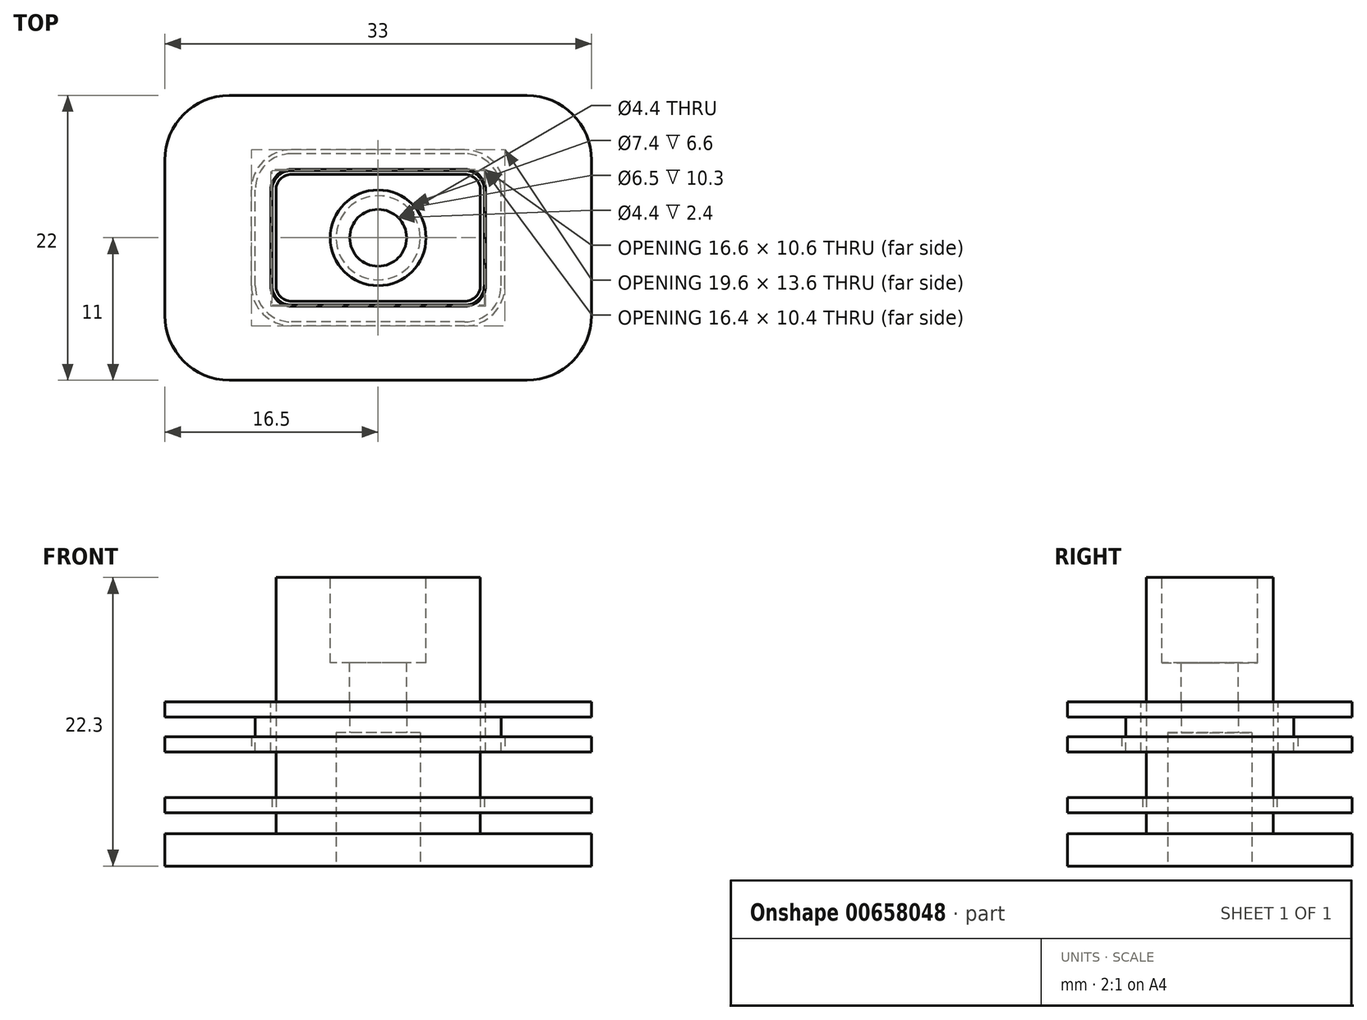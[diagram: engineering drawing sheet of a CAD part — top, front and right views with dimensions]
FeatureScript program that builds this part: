
annotation { "Feature Type Name" : "Feature", "Feature Type Description" : "" }
export const myFeature = defineFeature(function(context is Context, id is Id, definition is map)
    precondition{}
    {
        {
            var Q0;
            Q0=qCreatedBy(makeId("Top.planeOp"),FACE);
            var sketch = newSketch(context, id + "F0", { "sketchPlane" : qUnion([Q0])});
            skLineSegment(sketch, "E0.bottom", {"start": v(16.5, -11) * mm, "end": v(-16.5, -11) * mm});
            skLineSegment(sketch, "E0.top", {"start": v(16.5, 11) * mm, "end": v(-16.5, 11) * mm});
            skLineSegment(sketch, "E0.left", {"start": v(16.5, -11) * mm, "end": v(16.5, 11) * mm});
            skLineSegment(sketch, "E0.right", {"start": v(-16.5, -11) * mm, "end": v(-16.5, 11) * mm});
            skPoint(sketch, "E0.middle", {"position": v(0, 0) * mm});
            skLineSegment(sketch, "E1.bottom", {"start": v(7.9, -4.9) * mm, "end": v(-7.9, -4.9) * mm, "construction": true});
            skLineSegment(sketch, "E1.top", {"start": v(7.9, 4.9) * mm, "end": v(-7.9, 4.9) * mm, "construction": true});
            skLineSegment(sketch, "E1.left", {"start": v(7.9, -4.9) * mm, "end": v(7.9, 4.9) * mm, "construction": true});
            skLineSegment(sketch, "E1.right", {"start": v(-7.9, -4.9) * mm, "end": v(-7.9, 4.9) * mm, "construction": true});
            skCircle(sketch, "E2", {"center": v(0, 0) * mm, "radius": 3.25 * mm});
            skSolve(sketch);
        }
        {
            var Q0;
            Q0 = qSketchRegion(id + "F0", true);
            extrude(context, id + "F1", {"entities" : qUnion([Q0]), "depth" : 2.5 * mm, "offsetDistance" : 25 * mm});
        }
        {
            var Q0;
            Q0=makeQuery(id+"F1.opExtrude","CAP_FACE",FACE,{"disambiguationData":[OSD([sQuery(id+"F0.wireOp",EDGE,"E0.bottom"),sQuery(id+"F0.wireOp",EDGE,"E0.top"),sQuery(id+"F0.wireOp",EDGE,"E0.left"),sQuery(id+"F0.wireOp",EDGE,"E0.right"),sQuery(id+"F0.wireOp",EDGE,"E2")])],"isStart":false});
            var sketch = newSketch(context, id + "F2", { "sketchPlane" : qUnion([Q0])});
            skCircle(sketch, "E3.0", {"center": v(0, 0) * mm, "radius": 3.25 * mm});
            skLineSegment(sketch, "E4.0", {"start": v(7.9, 4.9) * mm, "end": v(-7.9, 4.9) * mm});
            skLineSegment(sketch, "E5.0", {"start": v(7.9, -4.9) * mm, "end": v(7.9, 4.9) * mm});
            skLineSegment(sketch, "E6.0", {"start": v(-7.9, -4.9) * mm, "end": v(-7.9, 4.9) * mm});
            skLineSegment(sketch, "E7.0", {"start": v(7.9, -4.9) * mm, "end": v(-7.9, -4.9) * mm});
            skSolve(sketch);
        }
        {
            var Q0;
            Q0 = qSketchRegion(id + "F2", true);
            extrude(context, id + "F3", {"entities" : qUnion([Q0]), "operationType" : NewBodyOperationType.ADD, "depth" : 7.8 * mm, "offsetDistance" : 25 * mm});
        }
        {
            var Q0;
            Q0=makeQuery(id+"F3.opExtrude","CAP_FACE",FACE,{"disambiguationData":[OSD([sQuery(id+"F2.wireOp",EDGE,"E3.0"),sQuery(id+"F2.wireOp",EDGE,"E4.0"),sQuery(id+"F2.wireOp",EDGE,"E5.0"),sQuery(id+"F2.wireOp",EDGE,"E6.0"),sQuery(id+"F2.wireOp",EDGE,"E7.0")])],"isStart":false});
            var sketch = newSketch(context, id + "F4", { "sketchPlane" : qUnion([Q0])});
            skLineSegment(sketch, "E8.0.0", {"start": v(-7.9, -4.9) * mm, "end": v(7.9, -4.9) * mm});
            skLineSegment(sketch, "E8.0.1", {"start": v(7.9, -4.9) * mm, "end": v(7.9, 4.9) * mm});
            skLineSegment(sketch, "E8.0.2", {"start": v(7.9, 4.9) * mm, "end": v(-7.9, 4.9) * mm});
            skLineSegment(sketch, "E8.0.3", {"start": v(-7.9, 4.9) * mm, "end": v(-7.9, -4.9) * mm});
            skCircle(sketch, "E9", {"center": v(0, 0) * mm, "radius": 2.2 * mm});
            skSolve(sketch);
        }
        {
            var Q0;
            Q0 = qSketchRegion(id + "F4", true);
            extrude(context, id + "F5", {"entities" : qUnion([Q0]), "operationType" : NewBodyOperationType.ADD, "depth" : 2.4 * mm, "offsetDistance" : 25 * mm});
        }
        {
            var Q0;
            Q0=makeQuery(id+"F5.opExtrude","CAP_FACE",FACE,{"disambiguationData":[OSD([sQuery(id+"F4.wireOp",EDGE,"E8.0.0"),sQuery(id+"F4.wireOp",EDGE,"E8.0.1"),sQuery(id+"F4.wireOp",EDGE,"E8.0.2"),sQuery(id+"F4.wireOp",EDGE,"E8.0.3"),sQuery(id+"F4.wireOp",EDGE,"E9")])],"isStart":false});
            var sketch = newSketch(context, id + "F6", { "sketchPlane" : qUnion([Q0])});
            skLineSegment(sketch, "E10.0.0", {"start": v(-7.9, -4.9) * mm, "end": v(7.9, -4.9) * mm});
            skLineSegment(sketch, "E10.0.1", {"start": v(7.9, -4.9) * mm, "end": v(7.9, 4.9) * mm});
            skLineSegment(sketch, "E10.0.2", {"start": v(7.9, 4.9) * mm, "end": v(-7.9, 4.9) * mm});
            skLineSegment(sketch, "E10.0.3", {"start": v(-7.9, 4.9) * mm, "end": v(-7.9, -4.9) * mm});
            skSolve(sketch);
        }
        {
            var Q0;
            Q0 = qSketchRegion(id + "F6", true);
            extrude(context, id + "F7", {"entities" : qUnion([Q0]), "depth" : 9.6 * mm, "offsetDistance" : 25 * mm});
        }
        {
            var Q0;
            Q0=makeQuery(id+"F7.opExtrude","CAP_FACE",FACE,{"disambiguationData":[OSD([sQuery(id+"F6.wireOp",EDGE,"E10.0.0"),sQuery(id+"F6.wireOp",EDGE,"E10.0.1"),sQuery(id+"F6.wireOp",EDGE,"E10.0.2"),sQuery(id+"F6.wireOp",EDGE,"E10.0.3")])],"isStart":false});
            var sketch = newSketch(context, id + "F8", { "sketchPlane" : qUnion([Q0])});
            skPoint(sketch, "E11", {"position": v(0, 0) * mm});
            skSolve(sketch);
        }
        {
            var Q0;
            Q0=sQuery(id+"F8.wireOp",VERTEX,"E11");
            var Q1;
            Q1=makeQuery(id+"F7.opExtrude","SWEPT_BODY",BODY,{"disambiguationData":[OSD([sQuery(id+"F6.wireOp",EDGE,"E10.0.0"),sQuery(id+"F6.wireOp",EDGE,"E10.0.1"),sQuery(id+"F6.wireOp",EDGE,"E10.0.2"),sQuery(id+"F6.wireOp",EDGE,"E10.0.3")])]});
            hole(context, id + "F9", {"style" : HoleStyle.C_BORE, "endStyle" : HoleEndStyle.THROUGH, "holeDiameter" : 4.4 * mm, "cBoreDiameter" : 7.4 * mm, "cBoreDepth" : 6.6 * mm, "majorDiameter" : 5 * mm, "tappedDepth" : 5 * mm, "tapClearance" : 6, "startFromSketch" : true, "locations" : qUnion([Q0]), "scope" : qUnion([Q1])});
        }
        {
            var Q0;
            Q0=makeQuery(id+"F1.opExtrude","SWEPT_EDGE",EDGE,{"disambiguationData":[OSD([sQuery(id+"F0.wireOp",EDGE,"E0.bottom"),sQuery(id+"F0.wireOp",EDGE,"E0.left")])]});
            var Q1;
            Q1=makeQuery(id+"F1.opExtrude","SWEPT_EDGE",EDGE,{"disambiguationData":[OSD([sQuery(id+"F0.wireOp",EDGE,"E0.top"),sQuery(id+"F0.wireOp",EDGE,"E0.left")])]});
            var Q2;
            Q2=makeQuery(id+"F1.opExtrude","SWEPT_EDGE",EDGE,{"disambiguationData":[OSD([sQuery(id+"F0.wireOp",EDGE,"E0.bottom"),sQuery(id+"F0.wireOp",EDGE,"E0.right")])]});
            var Q3;
            Q3=makeQuery(id+"F1.opExtrude","SWEPT_EDGE",EDGE,{"disambiguationData":[OSD([sQuery(id+"F0.wireOp",EDGE,"E0.top"),sQuery(id+"F0.wireOp",EDGE,"E0.right")])]});
            fillet(context, id + "F10", {"entities" : qUnion([Q0, Q1, Q2, Q3]), "radius" : 5 * mm, "tangentPropagation" : true, "allowEdgeOverflow" : false});
        }
        {
            var Q0;
            Q0=makeQuery(id+"F5.boolean.opBoolean","MERGE",EDGE,{"derivedFrom":[makeQuery(id+"F3.opExtrude","SWEPT_EDGE",EDGE,{"disambiguationData":[OSD([sQuery(id+"F2.wireOp",EDGE,"E4.0"),sQuery(id+"F2.wireOp",EDGE,"E6.0")])]}),makeQuery(id+"F5.opExtrude","SWEPT_EDGE",EDGE,{"disambiguationData":[OSD([sQuery(id+"F4.wireOp",EDGE,"E8.0.2"),sQuery(id+"F4.wireOp",EDGE,"E8.0.3")])]})]});
            var Q1;
            Q1=makeQuery(id+"F5.boolean.opBoolean","MERGE",EDGE,{"derivedFrom":[makeQuery(id+"F3.opExtrude","SWEPT_EDGE",EDGE,{"disambiguationData":[OSD([sQuery(id+"F2.wireOp",EDGE,"E6.0"),sQuery(id+"F2.wireOp",EDGE,"E7.0")])]}),makeQuery(id+"F5.opExtrude","SWEPT_EDGE",EDGE,{"disambiguationData":[OSD([sQuery(id+"F4.wireOp",EDGE,"E8.0.0"),sQuery(id+"F4.wireOp",EDGE,"E8.0.3")])]})]});
            var Q2;
            Q2=makeQuery(id+"F5.boolean.opBoolean","MERGE",EDGE,{"derivedFrom":[makeQuery(id+"F3.opExtrude","SWEPT_EDGE",EDGE,{"disambiguationData":[OSD([sQuery(id+"F2.wireOp",EDGE,"E4.0"),sQuery(id+"F2.wireOp",EDGE,"E5.0")])]}),makeQuery(id+"F5.opExtrude","SWEPT_EDGE",EDGE,{"disambiguationData":[OSD([sQuery(id+"F4.wireOp",EDGE,"E8.0.1"),sQuery(id+"F4.wireOp",EDGE,"E8.0.2")])]})]});
            var Q3;
            Q3=makeQuery(id+"F5.boolean.opBoolean","MERGE",EDGE,{"derivedFrom":[makeQuery(id+"F3.opExtrude","SWEPT_EDGE",EDGE,{"disambiguationData":[OSD([sQuery(id+"F2.wireOp",EDGE,"E5.0"),sQuery(id+"F2.wireOp",EDGE,"E7.0")])]}),makeQuery(id+"F5.opExtrude","SWEPT_EDGE",EDGE,{"disambiguationData":[OSD([sQuery(id+"F4.wireOp",EDGE,"E8.0.0"),sQuery(id+"F4.wireOp",EDGE,"E8.0.1")])]})]});
            var Q4;
            Q4=makeQuery(id+"F7.opExtrude","SWEPT_EDGE",EDGE,{"disambiguationData":[OSD([sQuery(id+"F6.wireOp",EDGE,"E10.0.1"),sQuery(id+"F6.wireOp",EDGE,"E10.0.2")])]});
            var Q5;
            Q5=makeQuery(id+"F7.opExtrude","SWEPT_EDGE",EDGE,{"disambiguationData":[OSD([sQuery(id+"F6.wireOp",EDGE,"E10.0.0"),sQuery(id+"F6.wireOp",EDGE,"E10.0.1")])]});
            var Q6;
            Q6=makeQuery(id+"F7.opExtrude","SWEPT_EDGE",EDGE,{"disambiguationData":[OSD([sQuery(id+"F6.wireOp",EDGE,"E10.0.2"),sQuery(id+"F6.wireOp",EDGE,"E10.0.3")])]});
            var Q7;
            Q7=makeQuery(id+"F7.opExtrude","SWEPT_EDGE",EDGE,{"disambiguationData":[OSD([sQuery(id+"F6.wireOp",EDGE,"E10.0.0"),sQuery(id+"F6.wireOp",EDGE,"E10.0.3")])]});
            fillet(context, id + "F11", {"entities" : qUnion([Q0, Q1, Q2, Q3, Q4, Q5, Q6, Q7]), "radius" : 1.2 * mm, "tangentPropagation" : true, "allowEdgeOverflow" : false});
        }
        {
            var Q0;
            Q0=makeQuery(id+"F5.opExtrude","CAP_FACE",FACE,{"disambiguationData":[OSD([sQuery(id+"F4.wireOp",EDGE,"E8.0.0"),sQuery(id+"F4.wireOp",EDGE,"E8.0.1"),sQuery(id+"F4.wireOp",EDGE,"E8.0.2"),sQuery(id+"F4.wireOp",EDGE,"E8.0.3"),sQuery(id+"F4.wireOp",EDGE,"E9")])],"isStart":false});
            var sketch = newSketch(context, id + "F12", { "sketchPlane" : qUnion([Q0])});
            skLineSegment(sketch, "E12.0", {"start": v(6.7, 5.3) * mm, "end": v(-6.7, 5.3) * mm});
            skArc(sketch, "E12.1", {"start": v(8.3, 3.7) * mm, "mid": v(7.83, 4.83) * mm, "end": v(6.7, 5.3) * mm});
            skArc(sketch, "E12.2", {"start": v(-6.7, 5.3) * mm, "mid": v(-7.83, 4.83) * mm, "end": v(-8.3, 3.7) * mm});
            skLineSegment(sketch, "E12.3", {"start": v(8.3, -3.7) * mm, "end": v(8.3, 3.7) * mm});
            skLineSegment(sketch, "E12.4", {"start": v(-8.3, -3.7) * mm, "end": v(-8.3, 3.7) * mm});
            skArc(sketch, "E12.5", {"start": v(-8.3, -3.7) * mm, "mid": v(-7.83, -4.83) * mm, "end": v(-6.7, -5.3) * mm});
            skLineSegment(sketch, "E12.6", {"start": v(6.7, -5.3) * mm, "end": v(-6.7, -5.3) * mm});
            skArc(sketch, "E12.7", {"start": v(6.7, -5.3) * mm, "mid": v(7.83, -4.83) * mm, "end": v(8.3, -3.7) * mm});
            skArc(sketch, "E13.0", {"start": v(-11.5, 11) * mm, "mid": v(-15.04, 9.54) * mm, "end": v(-16.5, 6) * mm});
            skLineSegment(sketch, "E14.0", {"start": v(11.5, 11) * mm, "end": v(-11.5, 11) * mm});
            skLineSegment(sketch, "E15.0", {"start": v(-16.5, -6) * mm, "end": v(-16.5, 6) * mm});
            skArc(sketch, "E16.0", {"start": v(16.5, 6) * mm, "mid": v(15.04, 9.54) * mm, "end": v(11.5, 11) * mm});
            skLineSegment(sketch, "E17.0", {"start": v(16.5, -6) * mm, "end": v(16.5, 6) * mm});
            skArc(sketch, "E18.0", {"start": v(11.5, -11) * mm, "mid": v(15.04, -9.54) * mm, "end": v(16.5, -6) * mm});
            skLineSegment(sketch, "E19.0", {"start": v(11.5, -11) * mm, "end": v(-11.5, -11) * mm});
            skArc(sketch, "E20.0", {"start": v(-16.5, -6) * mm, "mid": v(-15.04, -9.54) * mm, "end": v(-11.5, -11) * mm});
            skSolve(sketch);
        }
        {
            var Q0;
            Q0 = qSketchRegion(id + "F12", true);
            extrude(context, id + "F13", {"entities" : qUnion([Q0]), "oppositeDirection" : true, "depth" : 1.2 * mm, "offsetDistance" : 25 * mm});
        }
        {
            var Q0;
            Q0=makeQuery(id+"F13.opExtrude","CAP_FACE",FACE,{"disambiguationData":[OSD([sQuery(id+"F12.wireOp",EDGE,"E12.0"),sQuery(id+"F12.wireOp",EDGE,"E12.1"),sQuery(id+"F12.wireOp",EDGE,"E12.2"),sQuery(id+"F12.wireOp",EDGE,"E12.3"),sQuery(id+"F12.wireOp",EDGE,"E12.4"),sQuery(id+"F12.wireOp",EDGE,"E12.5"),sQuery(id+"F12.wireOp",EDGE,"E12.6"),sQuery(id+"F12.wireOp",EDGE,"E12.7"),sQuery(id+"F12.wireOp",EDGE,"E13.0"),sQuery(id+"F12.wireOp",EDGE,"E14.0"),sQuery(id+"F12.wireOp",EDGE,"E15.0"),sQuery(id+"F12.wireOp",EDGE,"E16.0"),sQuery(id+"F12.wireOp",EDGE,"E17.0"),sQuery(id+"F12.wireOp",EDGE,"E18.0"),sQuery(id+"F12.wireOp",EDGE,"E19.0"),sQuery(id+"F12.wireOp",EDGE,"E20.0")])],"isStart":false});
            var sketch = newSketch(context, id + "F14", { "sketchPlane" : qUnion([Q0])});
            skLineSegment(sketch, "E21.0", {"start": v(-9.5, 3.7) * mm, "end": v(-9.5, -3.7) * mm});
            skArc(sketch, "E21.1", {"start": v(-6.7, -6.5) * mm, "mid": v(-8.68, -5.68) * mm, "end": v(-9.5, -3.7) * mm});
            skArc(sketch, "E21.2", {"start": v(-9.5, 3.7) * mm, "mid": v(-8.68, 5.68) * mm, "end": v(-6.7, 6.5) * mm});
            skLineSegment(sketch, "E21.3", {"start": v(6.7, -6.5) * mm, "end": v(-6.7, -6.5) * mm});
            skLineSegment(sketch, "E21.4", {"start": v(6.7, 6.5) * mm, "end": v(-6.7, 6.5) * mm});
            skArc(sketch, "E21.5", {"start": v(6.7, 6.5) * mm, "mid": v(8.68, 5.68) * mm, "end": v(9.5, 3.7) * mm});
            skLineSegment(sketch, "E21.6", {"start": v(9.5, 3.7) * mm, "end": v(9.5, -3.7) * mm});
            skArc(sketch, "E21.7", {"start": v(9.5, -3.7) * mm, "mid": v(8.68, -5.68) * mm, "end": v(6.7, -6.5) * mm});
            skLineSegment(sketch, "E22.0", {"start": v(6.7, 5.3) * mm, "end": v(-6.7, 5.3) * mm});
            skArc(sketch, "E23.0", {"start": v(-8.3, 3.7) * mm, "mid": v(-7.83, 4.83) * mm, "end": v(-6.7, 5.3) * mm});
            skLineSegment(sketch, "E24.0", {"start": v(-8.3, 3.7) * mm, "end": v(-8.3, -3.7) * mm});
            skArc(sketch, "E25.0", {"start": v(-6.7, -5.3) * mm, "mid": v(-7.83, -4.83) * mm, "end": v(-8.3, -3.7) * mm});
            skLineSegment(sketch, "E26.0", {"start": v(6.7, -5.3) * mm, "end": v(-6.7, -5.3) * mm});
            skArc(sketch, "E27.0", {"start": v(8.3, -3.7) * mm, "mid": v(7.83, -4.83) * mm, "end": v(6.7, -5.3) * mm});
            skLineSegment(sketch, "E28.0", {"start": v(8.3, 3.7) * mm, "end": v(8.3, -3.7) * mm});
            skArc(sketch, "E29.0", {"start": v(6.7, 5.3) * mm, "mid": v(7.83, 4.83) * mm, "end": v(8.3, 3.7) * mm});
            skSolve(sketch);
        }
        {
            var Q0;
            Q0 = qSketchRegion(id + "F14", true);
            extrude(context, id + "F15", {"entities" : qUnion([Q0]), "operationType" : NewBodyOperationType.ADD, "depth" : 2.7 * mm, "offsetDistance" : 25 * mm});
        }
        {
            var Q0;
            Q0=makeQuery(id+"F15.opExtrude","CAP_FACE",FACE,{"disambiguationData":[OSD([sQuery(id+"F14.wireOp",EDGE,"E21.0"),sQuery(id+"F14.wireOp",EDGE,"E21.1"),sQuery(id+"F14.wireOp",EDGE,"E21.2"),sQuery(id+"F14.wireOp",EDGE,"E21.3"),sQuery(id+"F14.wireOp",EDGE,"E21.4"),sQuery(id+"F14.wireOp",EDGE,"E21.5"),sQuery(id+"F14.wireOp",EDGE,"E21.6"),sQuery(id+"F14.wireOp",EDGE,"E21.7"),sQuery(id+"F14.wireOp",EDGE,"E22.0"),sQuery(id+"F14.wireOp",EDGE,"E23.0"),sQuery(id+"F14.wireOp",EDGE,"E24.0"),sQuery(id+"F14.wireOp",EDGE,"E25.0"),sQuery(id+"F14.wireOp",EDGE,"E26.0"),sQuery(id+"F14.wireOp",EDGE,"E27.0"),sQuery(id+"F14.wireOp",EDGE,"E28.0"),sQuery(id+"F14.wireOp",EDGE,"E29.0")])],"isStart":false});
            var sketch = newSketch(context, id + "F16", { "sketchPlane" : qUnion([Q0])});
            skArc(sketch, "E30.0", {"start": v(6.7, 6.8) * mm, "mid": v(8.9, 5.9) * mm, "end": v(9.8, 3.7) * mm});
            skLineSegment(sketch, "E30.1", {"start": v(6.7, 6.8) * mm, "end": v(-6.7, 6.8) * mm});
            skLineSegment(sketch, "E30.2", {"start": v(9.8, 3.7) * mm, "end": v(9.8, -3.7) * mm});
            skArc(sketch, "E30.3", {"start": v(-9.8, 3.7) * mm, "mid": v(-8.9, 5.9) * mm, "end": v(-6.7, 6.8) * mm});
            skArc(sketch, "E30.4", {"start": v(9.8, -3.7) * mm, "mid": v(8.9, -5.9) * mm, "end": v(6.7, -6.8) * mm});
            skLineSegment(sketch, "E30.5", {"start": v(6.7, -6.8) * mm, "end": v(-6.7, -6.8) * mm});
            skArc(sketch, "E30.6", {"start": v(-6.7, -6.8) * mm, "mid": v(-8.9, -5.9) * mm, "end": v(-9.8, -3.7) * mm});
            skLineSegment(sketch, "E30.7", {"start": v(-9.8, 3.7) * mm, "end": v(-9.8, -3.7) * mm});
            skArc(sketch, "E31.0", {"start": v(-16.5, 6) * mm, "mid": v(-15.04, 9.54) * mm, "end": v(-11.5, 11) * mm});
            skLineSegment(sketch, "E32.0", {"start": v(-16.5, 6) * mm, "end": v(-16.5, -6) * mm});
            skLineSegment(sketch, "E33.0", {"start": v(11.5, 11) * mm, "end": v(-11.5, 11) * mm});
            skArc(sketch, "E34.0", {"start": v(11.5, 11) * mm, "mid": v(15.04, 9.54) * mm, "end": v(16.5, 6) * mm});
            skLineSegment(sketch, "E35.0", {"start": v(16.5, 6) * mm, "end": v(16.5, -6) * mm});
            skArc(sketch, "E36.0", {"start": v(16.5, -6) * mm, "mid": v(15.04, -9.54) * mm, "end": v(11.5, -11) * mm});
            skLineSegment(sketch, "E37.0", {"start": v(11.5, -11) * mm, "end": v(-11.5, -11) * mm});
            skArc(sketch, "E38.0", {"start": v(-11.5, -11) * mm, "mid": v(-15.04, -9.54) * mm, "end": v(-16.5, -6) * mm});
            skSolve(sketch);
        }
        {
            var Q0;
            Q0 = qSketchRegion(id + "F16", true);
            extrude(context, id + "F17", {"entities" : qUnion([Q0]), "oppositeDirection" : true, "depth" : 1.2 * mm, "offsetDistance" : 25 * mm});
        }
        {
            var Q0;
            Q0=makeQuery(id+"F1.opExtrude","CAP_FACE",FACE,{"disambiguationData":[OSD([sQuery(id+"F0.wireOp",EDGE,"E0.bottom"),sQuery(id+"F0.wireOp",EDGE,"E0.top"),sQuery(id+"F0.wireOp",EDGE,"E0.left"),sQuery(id+"F0.wireOp",EDGE,"E0.right"),sQuery(id+"F0.wireOp",EDGE,"E2")])],"isStart":false});
            cPlane(context, id + "F18", {"entities" : qUnion([Q0]), "cplaneType" : CPlaneType.OFFSET, "offset" : 1.6 * mm, "width" : 150 * mm, "height" : 150 * mm});
        }
        {
            var Q0;
            Q0=qCreatedBy(id+"F18.planeOp",FACE);
            var sketch = newSketch(context, id + "F19", { "sketchPlane" : qUnion([Q0])});
            skLineSegment(sketch, "E39.0", {"start": v(6.7, 5.2) * mm, "end": v(-6.7, 5.2) * mm});
            skArc(sketch, "E39.1", {"start": v(8.2, 3.7) * mm, "mid": v(7.76, 4.76) * mm, "end": v(6.7, 5.2) * mm});
            skArc(sketch, "E39.2", {"start": v(-6.7, 5.2) * mm, "mid": v(-7.76, 4.76) * mm, "end": v(-8.2, 3.7) * mm});
            skLineSegment(sketch, "E39.3", {"start": v(8.2, -3.7) * mm, "end": v(8.2, 3.7) * mm});
            skLineSegment(sketch, "E39.4", {"start": v(-8.2, -3.7) * mm, "end": v(-8.2, 3.7) * mm});
            skArc(sketch, "E39.5", {"start": v(-8.2, -3.7) * mm, "mid": v(-7.76, -4.76) * mm, "end": v(-6.7, -5.2) * mm});
            skLineSegment(sketch, "E39.6", {"start": v(6.7, -5.2) * mm, "end": v(-6.7, -5.2) * mm});
            skArc(sketch, "E39.7", {"start": v(6.7, -5.2) * mm, "mid": v(7.76, -4.76) * mm, "end": v(8.2, -3.7) * mm});
            skArc(sketch, "E40.0", {"start": v(-11.5, 11) * mm, "mid": v(-15.04, 9.54) * mm, "end": v(-16.5, 6) * mm});
            skLineSegment(sketch, "E41.0", {"start": v(11.5, 11) * mm, "end": v(-11.5, 11) * mm});
            skArc(sketch, "E42.0", {"start": v(16.5, 6) * mm, "mid": v(15.04, 9.54) * mm, "end": v(11.5, 11) * mm});
            skLineSegment(sketch, "E43.0", {"start": v(16.5, -6) * mm, "end": v(16.5, 6) * mm});
            skArc(sketch, "E44.0", {"start": v(11.5, -11) * mm, "mid": v(15.04, -9.54) * mm, "end": v(16.5, -6) * mm});
            skLineSegment(sketch, "E45.0", {"start": v(11.5, -11) * mm, "end": v(-11.5, -11) * mm});
            skArc(sketch, "E46.0", {"start": v(-16.5, -6) * mm, "mid": v(-15.04, -9.54) * mm, "end": v(-11.5, -11) * mm});
            skLineSegment(sketch, "E47.0", {"start": v(-16.5, -6) * mm, "end": v(-16.5, 6) * mm});
            skSolve(sketch);
        }
        {
            var Q0;
            Q0 = qSketchRegion(id + "F19", true);
            extrude(context, id + "F20", {"entities" : qUnion([Q0]), "depth" : 1.2 * mm, "offsetDistance" : 25 * mm});
        }
    });
